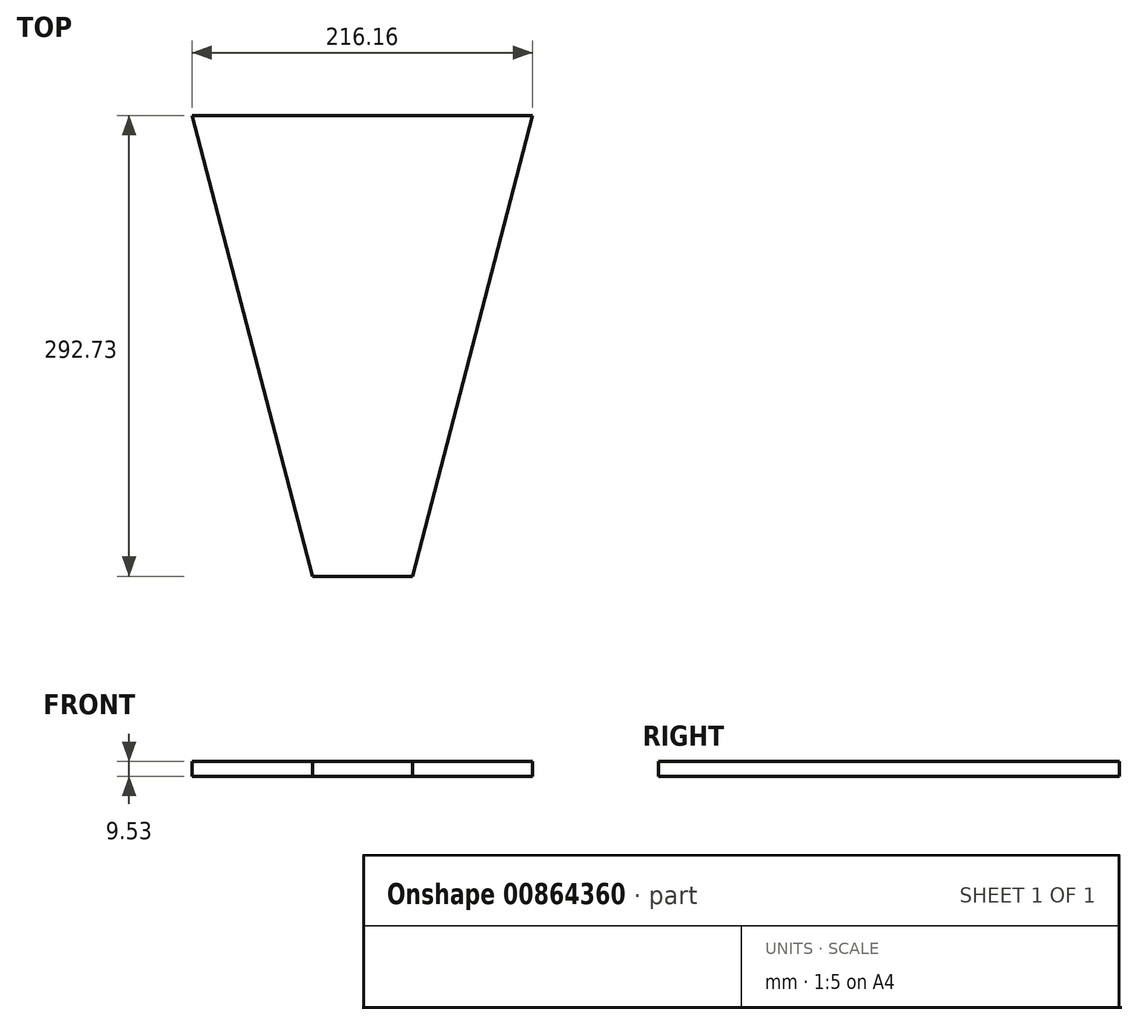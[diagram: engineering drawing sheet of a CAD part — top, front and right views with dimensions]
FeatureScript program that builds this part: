
annotation { "Feature Type Name" : "Feature", "Feature Type Description" : "" }
export const myFeature = defineFeature(function(context is Context, id is Id, definition is map)
    precondition{}
    {
        {
            var Q0;
            Q0=qCreatedBy(makeId("Top.planeOp"),FACE);
            var sketch = newSketch(context, id + "F0", { "sketchPlane" : qUnion([Q0])});
            skLineSegment(sketch, "E0", {"start": v(-31.75, -238.1) * mm, "end": v(0, -238.1) * mm});
            skLineSegment(sketch, "E1", {"start": v(0, 54.64) * mm, "end": v(-108.08, 54.64) * mm});
            skLineSegment(sketch, "E2", {"start": v(-108.08, 54.64) * mm, "end": v(-31.75, -238.1) * mm});
            skLineSegment(sketch, "E3.MirrorCS", {"start": v(0, 54.64) * mm, "end": v(108.08, 54.64) * mm});
            skLineSegment(sketch, "E4.MirrorCS", {"start": v(108.08, 54.64) * mm, "end": v(31.75, -238.1) * mm});
            skLineSegment(sketch, "E5.MirrorCS", {"start": v(31.75, -238.1) * mm, "end": v(0, -238.1) * mm});
            skSolve(sketch);
        }
        {
            var Q0;
            Q0 = qSketchRegion(id + "F0", true);
            extrude(context, id + "F1", {"entities" : qUnion([Q0]), "depth" : 9.52 * mm, "offsetDistance" : 25.4 * mm});
        }
    });
